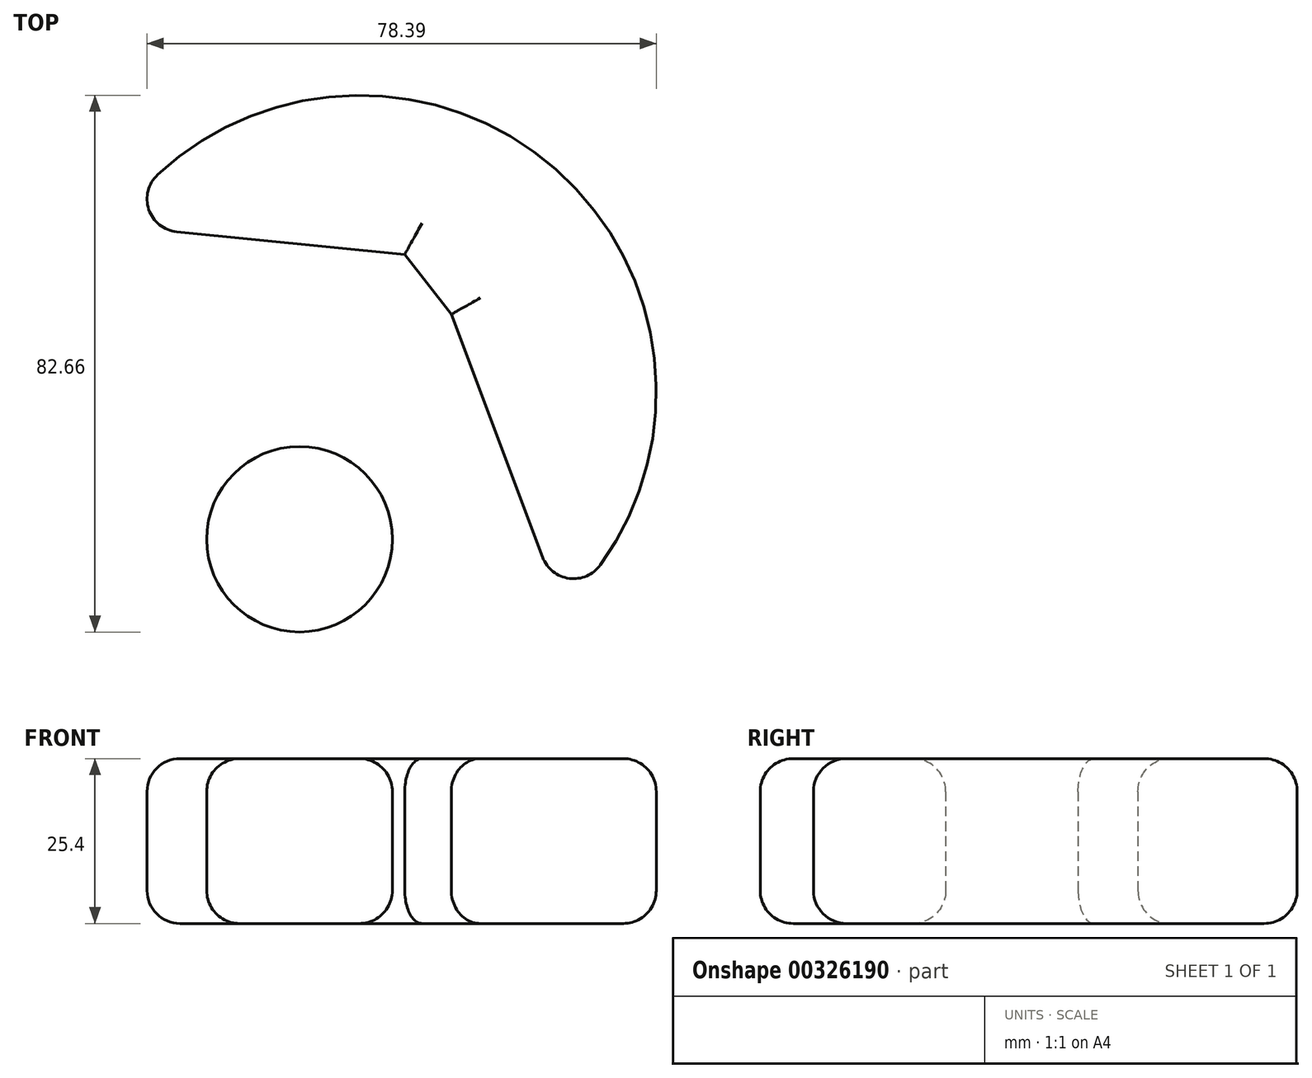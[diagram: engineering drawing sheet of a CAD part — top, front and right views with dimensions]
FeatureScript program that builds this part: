
annotation { "Feature Type Name" : "Feature", "Feature Type Description" : "" }
export const myFeature = defineFeature(function(context is Context, id is Id, definition is map)
    precondition{}
    {
        {
            var Q0;
            Q0=qCreatedBy(makeId("Top.planeOp"),FACE);
            var sketch = newSketch(context, id + "F0", { "sketchPlane" : qUnion([Q0])});
            skLineSegment(sketch, "E0", {"start": v(-61, 12.38) * mm, "end": v(-28.55, 48.33) * mm});
            skLineSegment(sketch, "E1", {"start": v(-28.54, 48.33) * mm, "end": v(16.2, 43.87) * mm});
            skLineSegment(sketch, "E2", {"start": v(23.36, 34.65) * mm, "end": v(40.4, -10.67) * mm});
            skLineSegment(sketch, "E3", {"start": v(23.36, 34.65) * mm, "end": v(16.2, 43.87) * mm});
            skLineSegment(sketch, "E4", {"start": v(40.4, -10.67) * mm, "end": v(-11.42, -39.3) * mm});
            skLineSegment(sketch, "E5", {"start": v(-11.42, -39.3) * mm, "end": v(-21.98, 5.2) * mm});
            skLineSegment(sketch, "E6", {"start": v(-21.98, 5.2) * mm, "end": v(-61, 12.38) * mm});
            skCircle(sketch, "E7", {"center": v(0, 0) * mm, "radius": 14.28 * mm});
            skArc(sketch, "E8", {"start": v(40.4, -10.67) * mm, "mid": v(38.95, 57.41) * mm, "end": v(-28.54, 48.33) * mm});
            skSolve(sketch);
        }
        {
            var Q0;
            Q0 = qSketchRegion(id + "F0", true);
            extrude(context, id + "F1", {"entities" : qUnion([Q0]), "depth" : 25.4 * mm});
        }
        {
            var Q0;
            Q0=makeQuery(id+"F1.opExtrude","CAP_FACE",FACE,{"disambiguationData":[OSD([sQuery(id+"F0.wireOp",EDGE,"E1"),sQuery(id+"F0.wireOp",EDGE,"E2"),sQuery(id+"F0.wireOp",EDGE,"E3"),sQuery(id+"F0.wireOp",EDGE,"E8")])],"isStart":false});
            var Q1;
            Q1=makeQuery(id+"F1.opExtrude","CAP_EDGE",EDGE,{"disambiguationData":[OSD([sQuery(id+"F0.wireOp",EDGE,"E2")])],"isStart":false});
            fillet(context, id + "F2", {"entities" : qUnion([Q0, Q1]), "radius" : 5.08 * mm, "tangentPropagation" : true, "allowEdgeOverflow" : false});
        }
        {
            var Q0;
            Q0=makeQuery(id+"F1.opExtrude","CAP_EDGE",EDGE,{"disambiguationData":[OSD([sQuery(id+"F0.wireOp",EDGE,"E7")])],"isStart":true});
            var Q1;
            Q1=makeQuery(id+"F1.opExtrude","CAP_EDGE",EDGE,{"disambiguationData":[OSD([sQuery(id+"F0.wireOp",EDGE,"E7")])],"isStart":false});
            var Q2;
            Q2=makeQuery(id+"F1.opExtrude","SWEPT_FACE",FACE,{"disambiguationData":[OSD([sQuery(id+"F0.wireOp",EDGE,"E7")])]});
            fillet(context, id + "F3", {"entities" : qUnion([Q0, Q1, Q2]), "radius" : 5.08 * mm, "tangentPropagation" : true, "allowEdgeOverflow" : false});
        }
        {
            var Q0;
            Q0=makeQuery(id+"F2.opFillet","BLEND_FACE",FACE,{"disambiguationData":[OSD([sQuery(id+"F0.wireOp",EDGE,"E8")])]});
            var Q1;
            Q1=makeQuery(id+"F1.opExtrude","CAP_EDGE",EDGE,{"disambiguationData":[OSD([sQuery(id+"F0.wireOp",EDGE,"E8")])],"isStart":true});
            var Q2;
            Q2=makeQuery(id+"F1.opExtrude","CAP_FACE",FACE,{"disambiguationData":[OSD([sQuery(id+"F0.wireOp",EDGE,"E1"),sQuery(id+"F0.wireOp",EDGE,"E2"),sQuery(id+"F0.wireOp",EDGE,"E3"),sQuery(id+"F0.wireOp",EDGE,"E8")])],"isStart":true});
            var Q3;
            {var subQ0=sQuery(id+"F0.wireOp",EDGE,"E8");Q3=makeQuery(id+"F2.opFillet","BLEND_EDGE",EDGE,{"blendedFrom":[makeQuery(id+"F1.opExtrude","CAP_EDGE",EDGE,{"disambiguationData":[OSD([subQ0])],"isStart":false}),makeQuery(id+"F1.opExtrude","SWEPT_FACE",FACE,{"disambiguationData":[OSD([subQ0])]})],"blendedInto":[makeQuery(id+"F1.opExtrude","SWEPT_FACE",FACE,{"disambiguationData":[OSD([subQ0])]})]});}
            fillet(context, id + "F4", {"entities" : qUnion([Q0, Q1, Q2, Q3]), "radius" : 5.08 * mm, "tangentPropagation" : true, "allowEdgeOverflow" : false});
        }
    });
